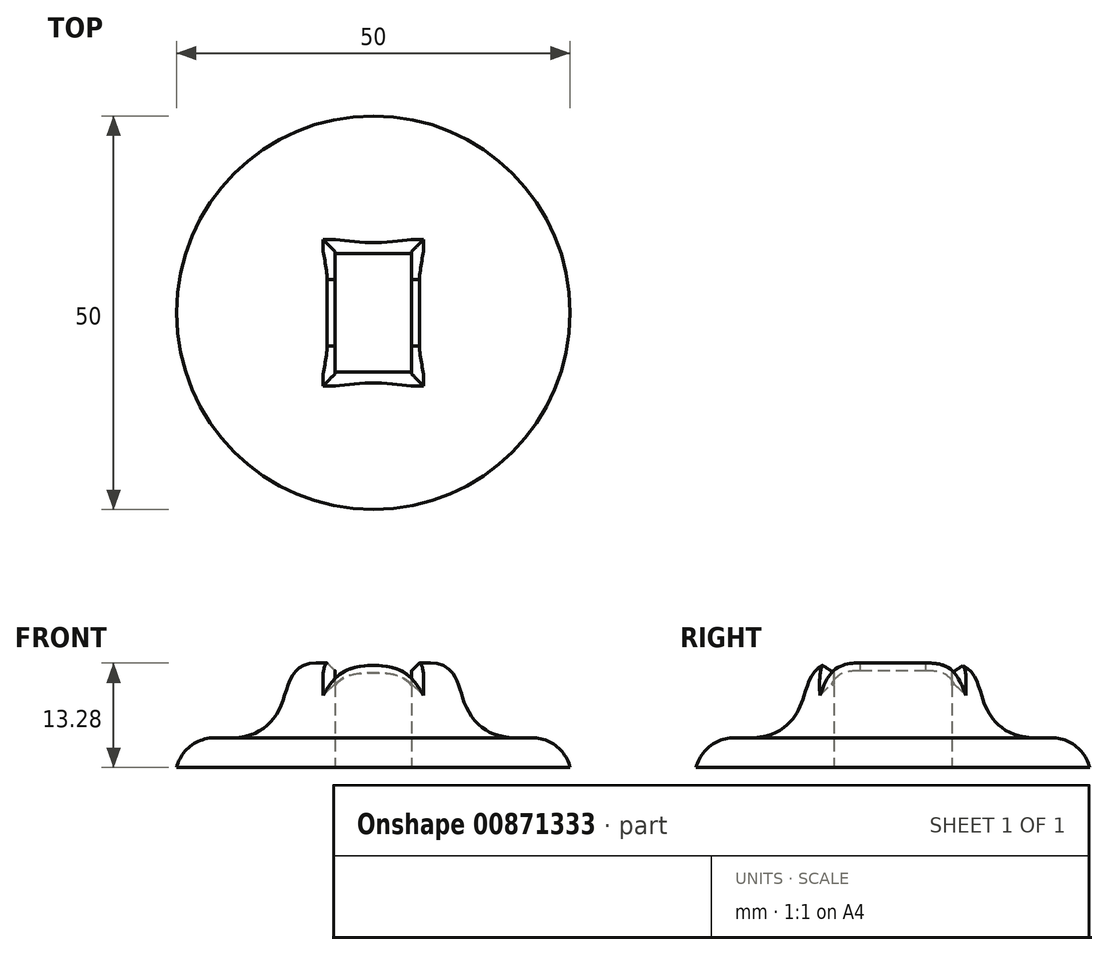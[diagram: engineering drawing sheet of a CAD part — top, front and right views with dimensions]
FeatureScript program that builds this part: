
annotation { "Feature Type Name" : "Feature", "Feature Type Description" : "" }
export const myFeature = defineFeature(function(context is Context, id is Id, definition is map)
    precondition{}
    {
        {
            var Q0;
            Q0=qCreatedBy(makeId("Front.planeOp"),FACE);
            var sketch = newSketch(context, id + "F0", { "sketchPlane" : qUnion([Q0])});
            skLineSegment(sketch, "E0", {"start": v(-25, 0) * mm, "end": v(-25, 4) * mm});
            skFitSpline(sketch, "E1", {"points": [v(-25, 4) * mm, v(-16.2, 4) * mm, v(-11.6, 8.16) * mm, v(-7.2, 13.28) * mm], "startDerivative": vector(18.78, 1.3) * mm, "endDerivative": vector(31.81, -0.33) * mm});
            skLineSegment(sketch, "E2", {"start": v(0, 0) * mm, "end": v(0, 13.28) * mm});
            skLineSegment(sketch, "E3", {"start": v(0, 13.28) * mm, "end": v(-7.2, 13.28) * mm});
            skLineSegment(sketch, "E4", {"start": v(0, 0) * mm, "end": v(-25, 0) * mm});
            skSolve(sketch);
        }
        {
            var Q0;
            Q0=makeQuery(id+"F0.imprint","IMPRINT",FACE,{"disambiguationData":[TD([[makeQuery(id+"F0.imprint","IMPRINT",EDGE,{"derivedFrom":sQuery(id+"F0.wireOp",EDGE,"E0")}),-1.0]])]});
            var Q1;
            Q1=sQuery(id+"F0.wireOp",EDGE,"E2");
            revolve(context, id + "F1", {"surfaceOperationType" : NewSurfaceOperationType.NEW, "entities" : qUnion([Q0]), "axis" : qUnion([Q1]), "revolveType" : RevolveType.FULL});
        }
        {
            var Q0;
            Q0=makeQuery(id+"F1.opRevolve","SWEPT_FACE",FACE,{"disambiguationData":[OSD([sQuery(id+"F0.wireOp",EDGE,"E4")])]});
            var sketch = newSketch(context, id + "F2", { "sketchPlane" : qUnion([Q0])});
            skLineSegment(sketch, "E5.bottom", {"start": v(-4.85, 7.5) * mm, "end": v(4.85, 7.5) * mm});
            skLineSegment(sketch, "E5.top", {"start": v(-4.85, -7.5) * mm, "end": v(4.85, -7.5) * mm});
            skLineSegment(sketch, "E5.left", {"start": v(-4.85, 7.5) * mm, "end": v(-4.85, -7.5) * mm});
            skLineSegment(sketch, "E5.right", {"start": v(4.85, 7.5) * mm, "end": v(4.85, -7.5) * mm});
            skSolve(sketch);
        }
        {
            var Q0;
            Q0=makeQuery(id+"F2.imprint","IMPRINT",FACE,{"disambiguationData":[TD([[makeQuery(id+"F2.imprint","IMPRINT",EDGE,{"derivedFrom":sQuery(id+"F2.wireOp",EDGE,"E5.bottom")}),-1.0]])]});
            extrude(context, id + "F3", {"entities" : qUnion([Q0]), "operationType" : NewBodyOperationType.REMOVE, "endBound" : BoundingType.THROUGH_ALL, "oppositeDirection" : true, "depth" : 25 * mm, "offsetDistance" : 25 * mm});
        }
        {
            var Q0;
            Q0=makeQuery(id+"F3.boolean.opBoolean","INTERSECT",EDGE,{"derivedFrom":[makeQuery(id+"F1.opRevolve","SWEPT_FACE",FACE,{"disambiguationData":[OSD([sQuery(id+"F0.wireOp",EDGE,"E3")])]}),makeQuery(id+"F3.opExtrude","SWEPT_FACE",FACE,{"disambiguationData":[OSD([sQuery(id+"F2.wireOp",EDGE,"E5.left")])]})]});
            var Q1;
            Q1=makeQuery(id+"F3.boolean.opBoolean","INTERSECT",EDGE,{"derivedFrom":[makeQuery(id+"F1.opRevolve","SWEPT_FACE",FACE,{"disambiguationData":[OSD([sQuery(id+"F0.wireOp",EDGE,"E1")])]}),makeQuery(id+"F3.opExtrude","SWEPT_FACE",FACE,{"disambiguationData":[OSD([sQuery(id+"F2.wireOp",EDGE,"E5.top")])]})]});
            var Q2;
            Q2=makeQuery(id+"F3.boolean.opBoolean","INTERSECT",EDGE,{"derivedFrom":[makeQuery(id+"F1.opRevolve","SWEPT_FACE",FACE,{"disambiguationData":[OSD([sQuery(id+"F0.wireOp",EDGE,"E1")])]}),makeQuery(id+"F3.opExtrude","SWEPT_FACE",FACE,{"disambiguationData":[OSD([sQuery(id+"F2.wireOp",EDGE,"E5.bottom")])]})]});
            var Q3;
            Q3=makeQuery(id+"F3.boolean.opBoolean","INTERSECT",EDGE,{"derivedFrom":[makeQuery(id+"F1.opRevolve","SWEPT_FACE",FACE,{"disambiguationData":[OSD([sQuery(id+"F0.wireOp",EDGE,"E3")])]}),makeQuery(id+"F3.opExtrude","SWEPT_FACE",FACE,{"disambiguationData":[OSD([sQuery(id+"F2.wireOp",EDGE,"E5.right")])]})]});
            chamfer(context, id + "F4", {"entities" : qUnion([Q0, Q1, Q2, Q3]), "width" : 1 * mm, "tangentPropagation" : true});
        }
        {
            var Q0;
            Q0=makeQuery(id+"F1.opRevolve","SWEPT_EDGE",EDGE,{"disambiguationData":[OSD([sQuery(id+"F0.wireOp",EDGE,"E0"),sQuery(id+"F0.wireOp",EDGE,"E1")])]});
            fillet(context, id + "F5", {"entities" : qUnion([Q0]), "radius" : 5 * mm, "tangentPropagation" : true, "allowEdgeOverflow" : false});
        }
    });
